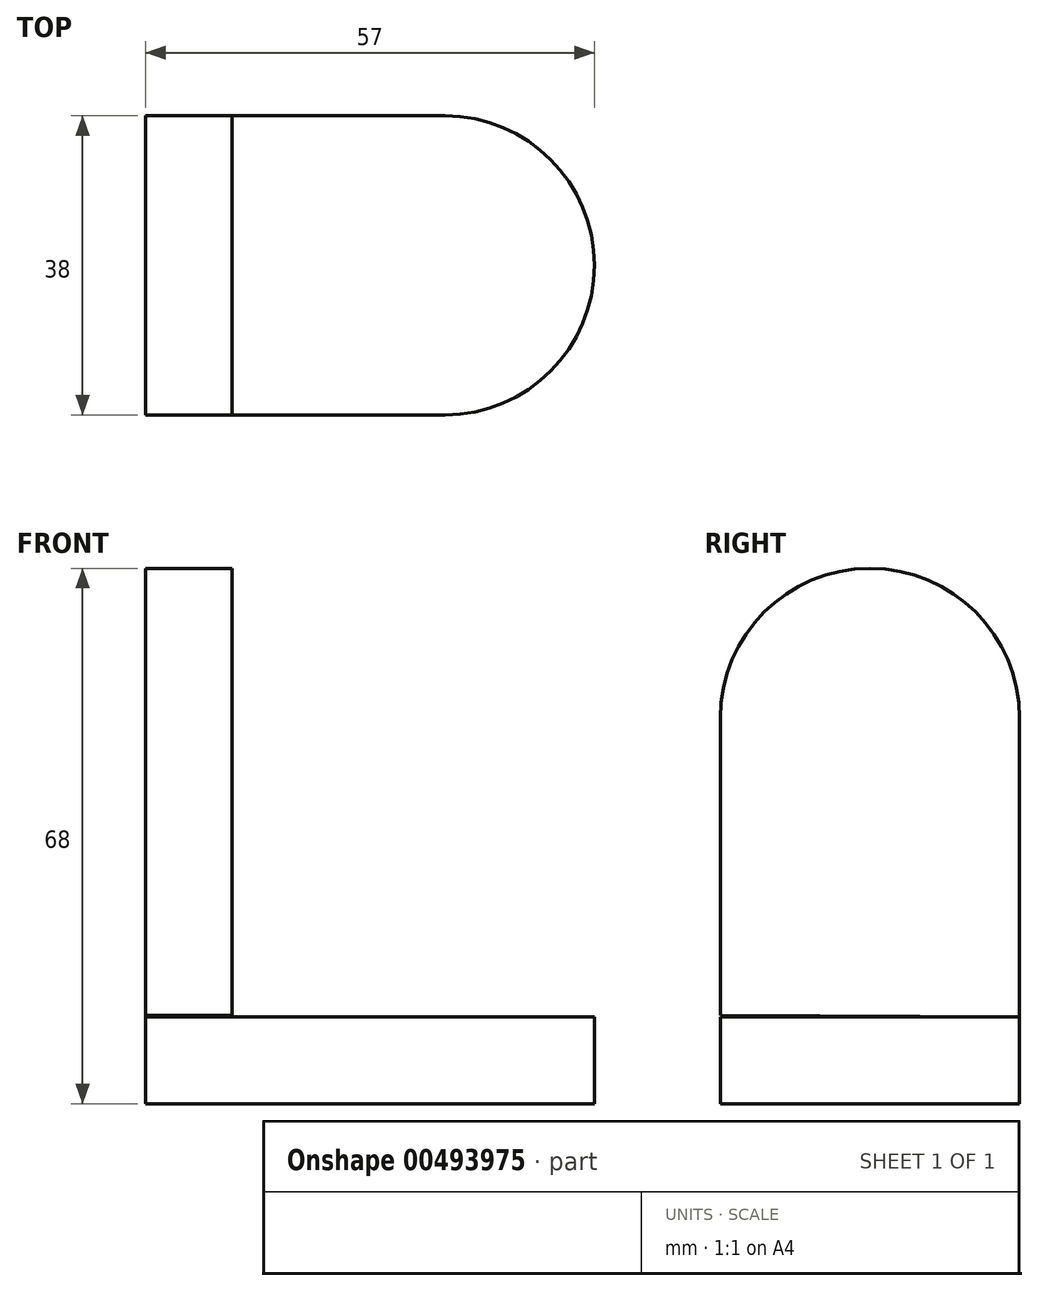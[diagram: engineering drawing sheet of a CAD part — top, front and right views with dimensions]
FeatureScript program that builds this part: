
annotation { "Feature Type Name" : "Feature", "Feature Type Description" : "" }
export const myFeature = defineFeature(function(context is Context, id is Id, definition is map)
    precondition{}
    {
        {
            var Q0;
            Q0=qCreatedBy(makeId("Top.planeOp"),FACE);
            var sketch = newSketch(context, id + "F0", { "sketchPlane" : qUnion([Q0])});
            skLineSegment(sketch, "E0", {"start": v(0, 0) * mm, "end": v(38, 0) * mm});
            skLineSegment(sketch, "E1", {"start": v(0, 38) * mm, "end": v(38, 38) * mm});
            skArc(sketch, "E2", {"start": v(38, 0) * mm, "mid": v(57, 19) * mm, "end": v(38, 38) * mm});
            skLineSegment(sketch, "E3", {"start": v(0, 38) * mm, "end": v(0, 0) * mm});
            skSolve(sketch);
        }
        {
            var Q0;
            Q0=makeQuery(id+"F0.imprint","IMPRINT",FACE,{"disambiguationData":[TD([[makeQuery(id+"F0.imprint","IMPRINT",EDGE,{"derivedFrom":sQuery(id+"F0.wireOp",EDGE,"E0")}),1.0]])]});
            extrude(context, id + "F1", {"entities" : qUnion([Q0]), "depth" : 11 * mm});
        }
        {
            var Q0;
            Q0=qCreatedBy(makeId("Right.planeOp"),FACE);
            var sketch = newSketch(context, id + "F2", { "sketchPlane" : qUnion([Q0])});
            skLineSegment(sketch, "E4", {"start": v(0, 11.2) * mm, "end": v(0, 49.2) * mm});
            skLineSegment(sketch, "E5", {"start": v(38, 11) * mm, "end": v(38, 49) * mm});
            skArc(sketch, "E6", {"start": v(38, 49) * mm, "mid": v(19, 68) * mm, "end": v(0, 49) * mm});
            skLineSegment(sketch, "E7", {"start": v(0, 11.2) * mm, "end": v(38, 11) * mm});
            skSolve(sketch);
        }
        {
            var Q0;
            Q0 = qSketchRegion(id + "F2", true);
            extrude(context, id + "F3", {"entities" : qUnion([Q0]), "depth" : 11 * mm});
        }
    });
